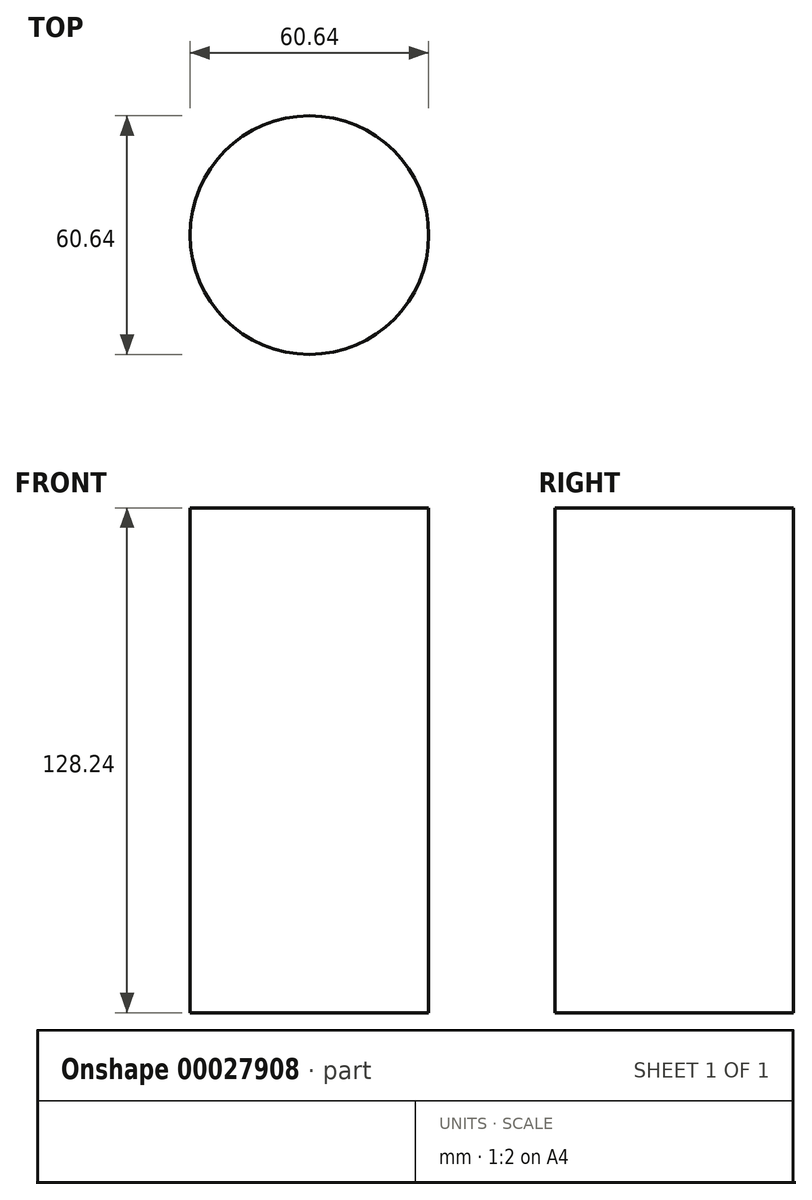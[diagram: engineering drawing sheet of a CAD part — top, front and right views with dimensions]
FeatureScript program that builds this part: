
annotation { "Feature Type Name" : "Feature", "Feature Type Description" : "" }
export const myFeature = defineFeature(function(context is Context, id is Id, definition is map)
    precondition{}
    {
        {
            var Q0;
            Q0=qCreatedBy(makeId("Top.planeOp"),FACE);
            var sketch = newSketch(context, id + "F0", { "sketchPlane" : qUnion([Q0])});
            skCircle(sketch, "E0", {"center": v(0, 0) * mm, "radius": 30.31 * mm});
            skSolve(sketch);
        }
        {
            var Q0;
            Q0 = qSketchRegion(id + "F0", true);
            extrude(context, id + "F1", {"entities" : qUnion([Q0]), "depth" : 128.24 * mm});
        }
    });
